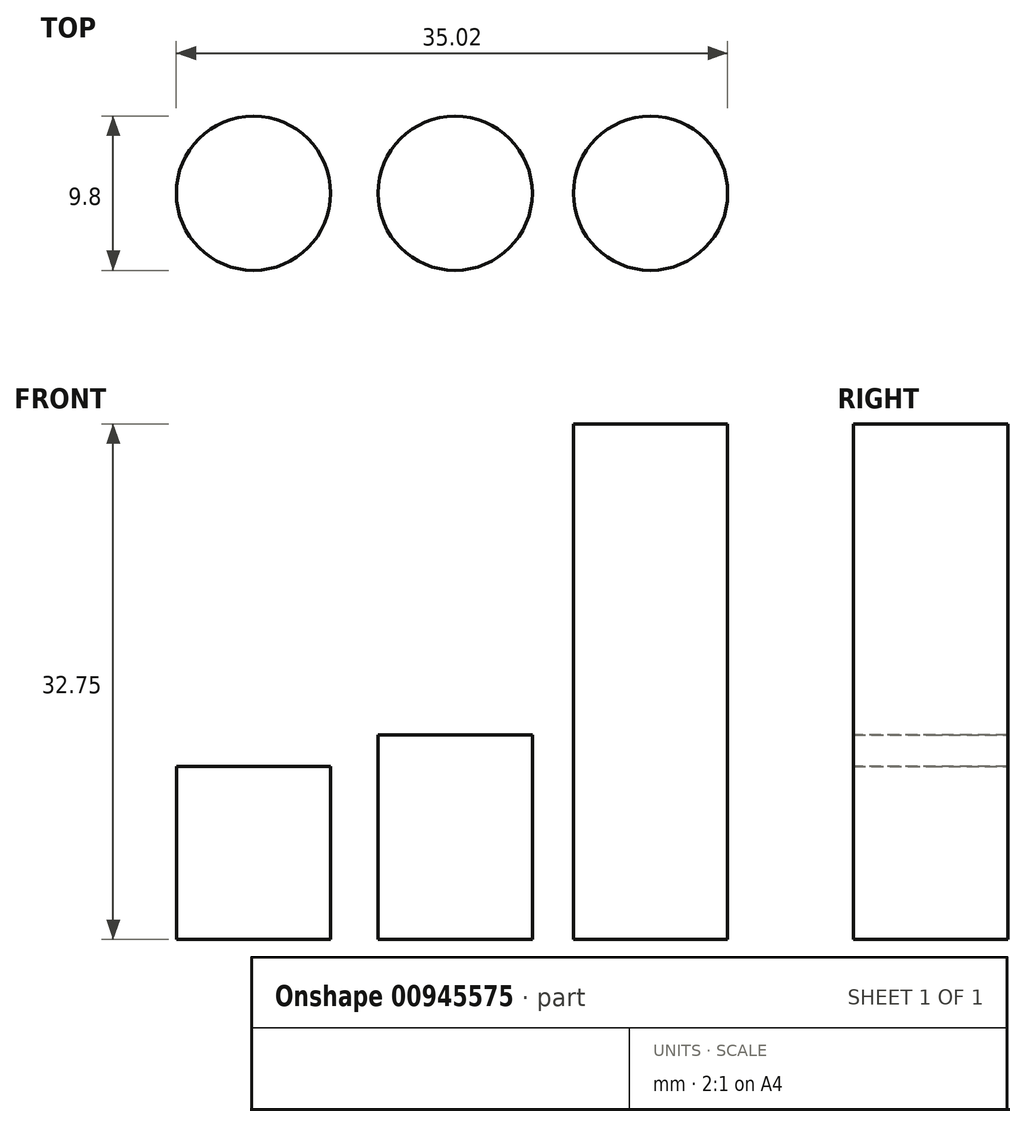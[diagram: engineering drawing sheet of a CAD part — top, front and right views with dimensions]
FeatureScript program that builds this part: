
annotation { "Feature Type Name" : "Feature", "Feature Type Description" : "" }
export const myFeature = defineFeature(function(context is Context, id is Id, definition is map)
    precondition{}
    {
        {
            var Q0;
            Q0=qCreatedBy(makeId("Top.planeOp"),FACE);
            var sketch = newSketch(context, id + "F0", { "sketchPlane" : qUnion([Q0])});
            skCircle(sketch, "E0", {"center": v(-39.33, 13.28) * mm, "radius": 4.9 * mm});
            skCircle(sketch, "E1", {"center": v(-26.52, 13.28) * mm, "radius": 4.9 * mm});
            skCircle(sketch, "E2", {"center": v(-14.1, 13.28) * mm, "radius": 4.9 * mm});
            skCircle(sketch, "E3", {"center": v(-39.33, 13.28) * mm, "radius": 4.1 * mm, "construction": true});
            skSolve(sketch);
        }
        {
            var Q0;
            Q0=makeQuery(id+"F0.imprint","IMPRINT",FACE,{"disambiguationData":[TD([[makeQuery(id+"F0.imprint","IMPRINT",EDGE,{"derivedFrom":sQuery(id+"F0.wireOp",EDGE,"E0")}),1.0]])]});
            extrude(context, id + "F1", {"entities" : qUnion([Q0]), "depth" : 11 * mm, "offsetDistance" : 25 * mm});
        }
        {
            var Q0;
            Q0=makeQuery(id+"F0.imprint","IMPRINT",FACE,{"disambiguationData":[TD([[makeQuery(id+"F0.imprint","IMPRINT",EDGE,{"derivedFrom":sQuery(id+"F0.wireOp",EDGE,"E1")}),1.0]])]});
            var Q1;
            Q1=sQuery(id+"F0.wireOp",EDGE,"E1");
            extrude(context, id + "F2", {"entities" : qUnion([Q0]), "surfaceEntities" : qUnion([Q1]), "depth" : 13 * mm, "offsetDistance" : 25 * mm});
        }
        {
            var Q0;
            Q0=makeQuery(id+"F0.imprint","IMPRINT",FACE,{"disambiguationData":[TD([[makeQuery(id+"F0.imprint","IMPRINT",EDGE,{"derivedFrom":sQuery(id+"F0.wireOp",EDGE,"E2")}),1.0]])]});
            extrude(context, id + "F3", {"entities" : qUnion([Q0]), "depth" : 32.75 * mm, "offsetDistance" : 25 * mm});
        }
    });
